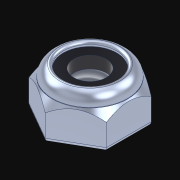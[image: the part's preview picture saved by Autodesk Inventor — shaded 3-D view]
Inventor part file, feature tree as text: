
AUTODESK INVENTOR PART (.ipt)
format: ipt  version: 2021.3 (Build 253353010, 353A)  size: 214,528 bytes
history: native  units: in
note: dims shown in document units (in); Inventor stores cm internally (conversion verified against a paired STEP export)
features: split x2, sketch x2, other x1, imported_body x1, plane x1, thread x1, extrude x1, fillet x1, projected_geometry x1
ambient origin geometry x8: Origin, YZ Plane, XZ Plane, XY Plane, X Axis, Y Axis, Z Axis, Center Point
bodies: Body1 (feature_tree)
feature tree (11):
  parser-record x1  (decoder bookkeeping rows leaked as tree rows — omitted from the tree; the rows remain in map.json)
  imported_body  "Base1"
  plane  "Work Plane1"
  split  "Split1"
  thread  "Thread1"  [1 undecoded]
  split  "Split2"
  extrude  "Extrusion1"  Depth=0.015in TaperAngle=0.0deg
  fillet  "Fillet1"  Radius=0.015in
  sketch  "Sketch1"  dims[d2=-0.05in d5=0.016in d6=0.0in d7=0.015in]
  sketch  "Sketch2"
  projected_geometry  "Projected Loop1"
note: 1 required parameter value undecoded (feature->parameter linkage not recoverable at this tier; creation-order binding heuristic only, values carry confidence <= 0.55)
